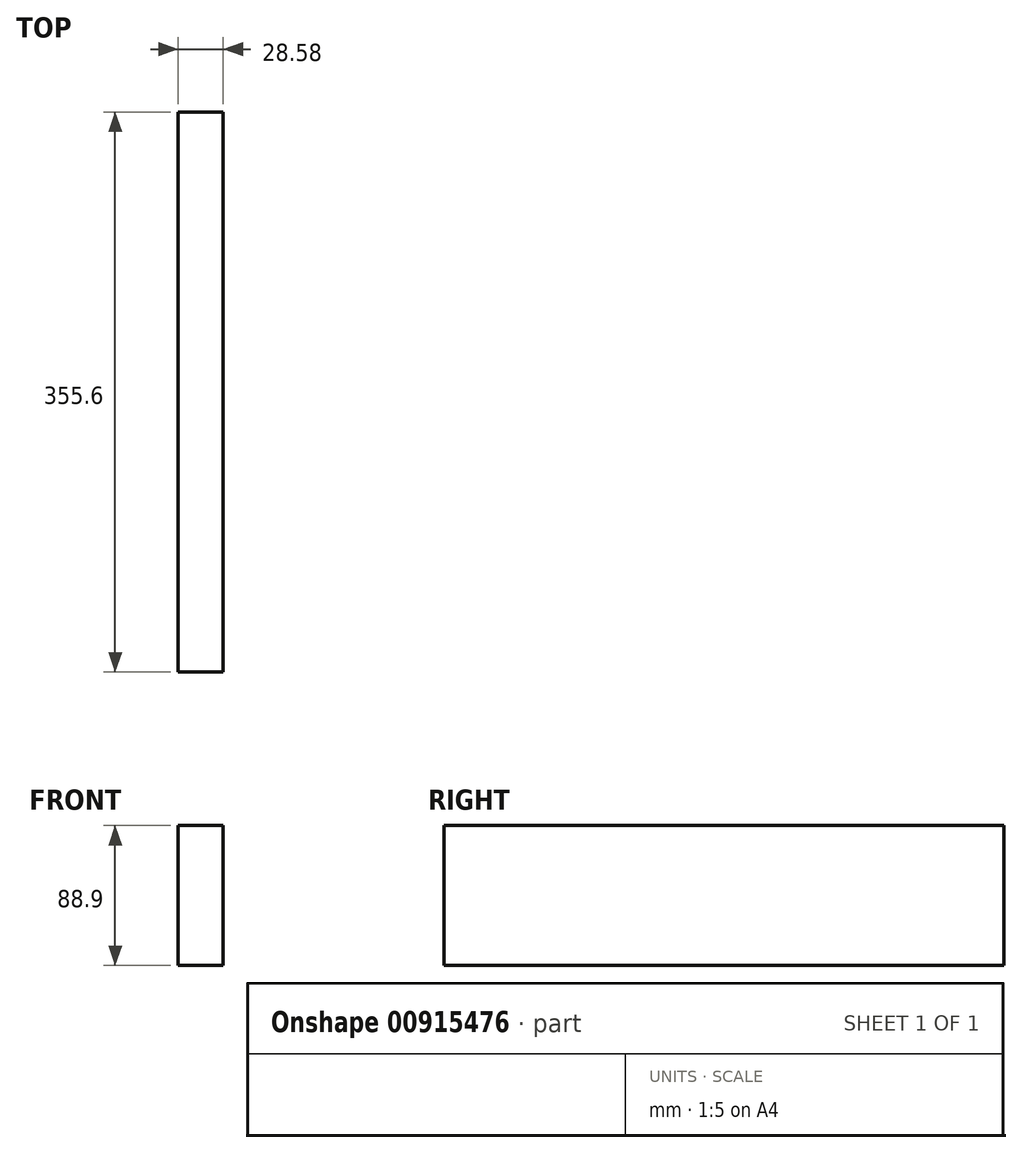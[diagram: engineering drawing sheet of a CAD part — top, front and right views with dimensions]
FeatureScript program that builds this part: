
annotation { "Feature Type Name" : "Feature", "Feature Type Description" : "" }
export const myFeature = defineFeature(function(context is Context, id is Id, definition is map)
    precondition{}
    {
        {
            var Q0;
            Q0=qCreatedBy(makeId("Front.planeOp"),FACE);
            var sketch = newSketch(context, id + "F0", { "sketchPlane" : qUnion([Q0])});
            skLineSegment(sketch, "E0.bottom", {"start": v(-14.29, 44.45) * mm, "end": v(14.29, 44.45) * mm});
            skLineSegment(sketch, "E0.top", {"start": v(-14.29, -44.45) * mm, "end": v(14.29, -44.45) * mm});
            skLineSegment(sketch, "E0.left", {"start": v(-14.29, 44.45) * mm, "end": v(-14.29, -44.45) * mm});
            skLineSegment(sketch, "E0.right", {"start": v(14.29, 44.45) * mm, "end": v(14.29, -44.45) * mm});
            skPoint(sketch, "E0.middle", {"position": v(0, 0) * mm});
            skSolve(sketch);
        }
        {
            var Q0;
            Q0=makeQuery(id+"F0.imprint","IMPRINT",FACE,{"disambiguationData":[TD([[makeQuery(id+"F0.imprint","IMPRINT",EDGE,{"derivedFrom":sQuery(id+"F0.wireOp",EDGE,"E0.bottom")}),-1.0]])]});
            extrude(context, id + "F1", {"entities" : qUnion([Q0]), "depth" : 355.6 * mm, "offsetDistance" : 25.4 * mm});
        }
    });
